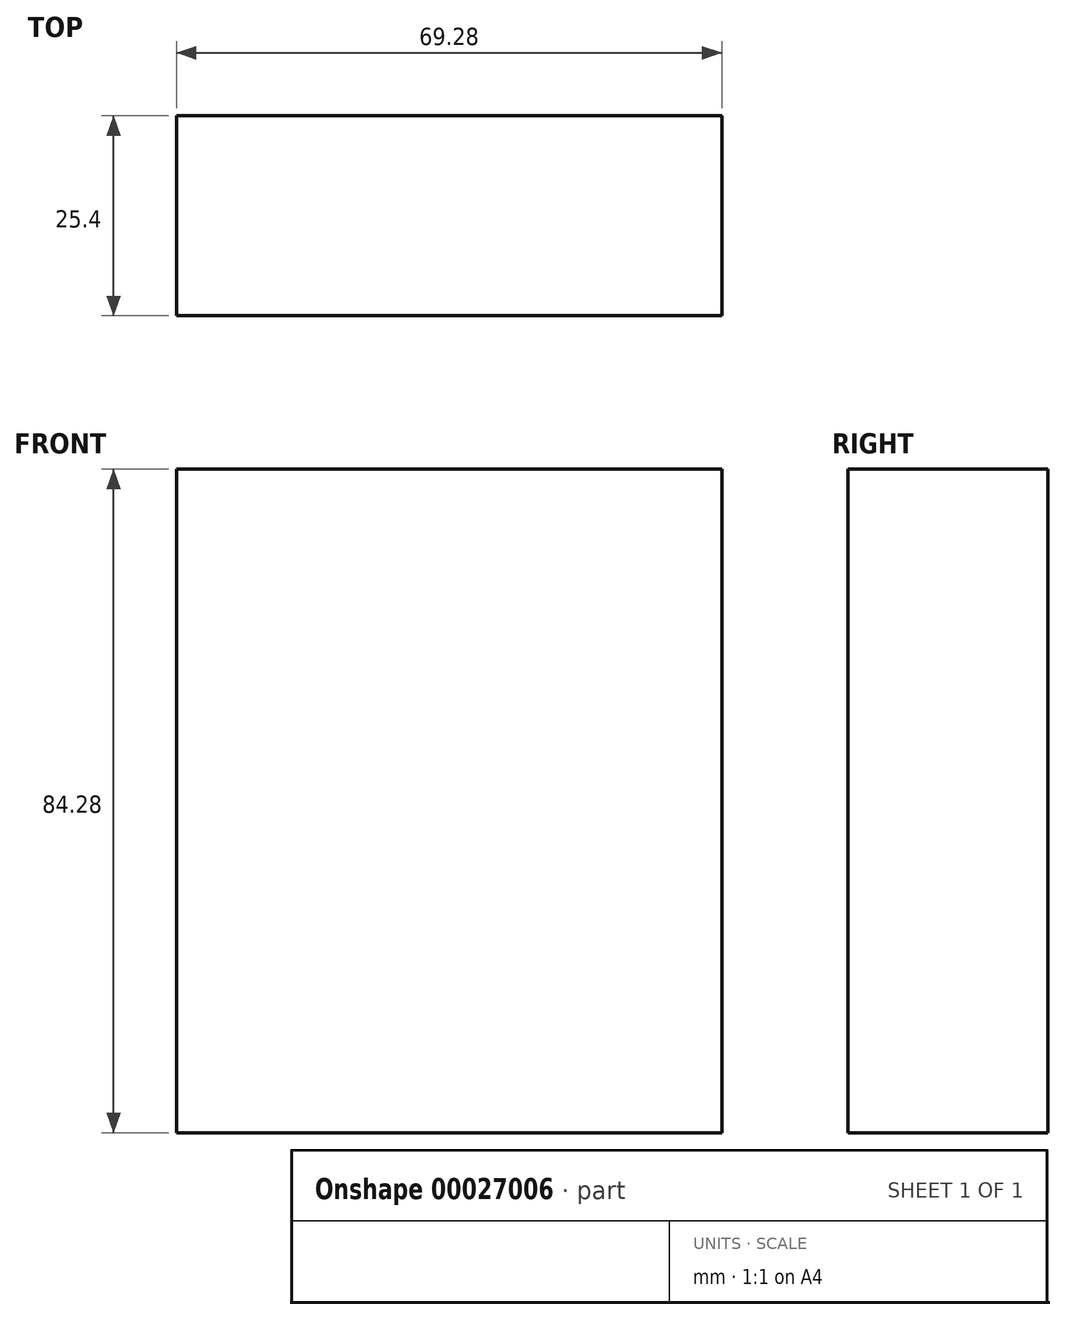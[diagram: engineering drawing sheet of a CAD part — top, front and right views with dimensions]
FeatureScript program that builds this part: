
annotation { "Feature Type Name" : "Feature", "Feature Type Description" : "" }
export const myFeature = defineFeature(function(context is Context, id is Id, definition is map)
    precondition{}
    {
        {
            var Q0;
            Q0=qCreatedBy(makeId("Front.planeOp"),FACE);
            var sketch = newSketch(context, id + "F0", { "sketchPlane" : qUnion([Q0])});
            skLineSegment(sketch, "E0.bottom", {"start": v(-34.4, 47.68) * mm, "end": v(34.87, 47.68) * mm});
            skLineSegment(sketch, "E0.top", {"start": v(-34.4, -36.6) * mm, "end": v(34.87, -36.6) * mm});
            skLineSegment(sketch, "E0.left", {"start": v(-34.4, 47.68) * mm, "end": v(-34.4, -36.6) * mm});
            skLineSegment(sketch, "E0.right", {"start": v(34.87, 47.68) * mm, "end": v(34.87, -36.6) * mm});
            skSolve(sketch);
        }
        {
            var Q0;
            Q0=makeQuery(id+"F0.imprint","IMPRINT",FACE,{"disambiguationData":[TD([[makeQuery(id+"F0.imprint","IMPRINT",EDGE,{"derivedFrom":sQuery(id+"F0.wireOp",EDGE,"E0.bottom")}),-1.0]])]});
            extrude(context, id + "F1", {"entities" : qUnion([Q0]), "depth" : 25.4 * mm});
        }
    });
